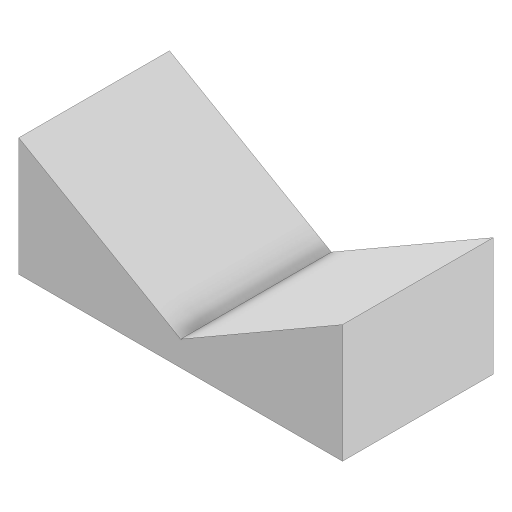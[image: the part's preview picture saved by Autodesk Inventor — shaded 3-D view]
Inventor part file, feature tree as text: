
AUTODESK INVENTOR PART (.ipt)
format: ipt  version: 2023.3 (Build 273359000, 359)  size: 110,592 bytes
history: native  units: mm
features: extrude x2, sketch x2
ambient origin geometry x8: Origin, YZ Plane, XZ Plane, XY Plane, X Axis, Y Axis, Z Axis, Center Point
bodies: Solid1 (feature_tree)
feature tree (4):
  extrude  "Extrusion1"  Depth=5.8mm
  extrude  "Extrusion2"  Depth=2.7mm TaperAngle=0.0deg
  sketch  "Sketch1"  dims[d0=5.5mm d1=5.8mm]
  sketch  "Sketch2"  dims[d2=5.121mm d3=2.7mm d4=0.0mm d5=1.0mm d6=1.0mm d7=2.0mm d8=0.7mm d9=0.0mm]
